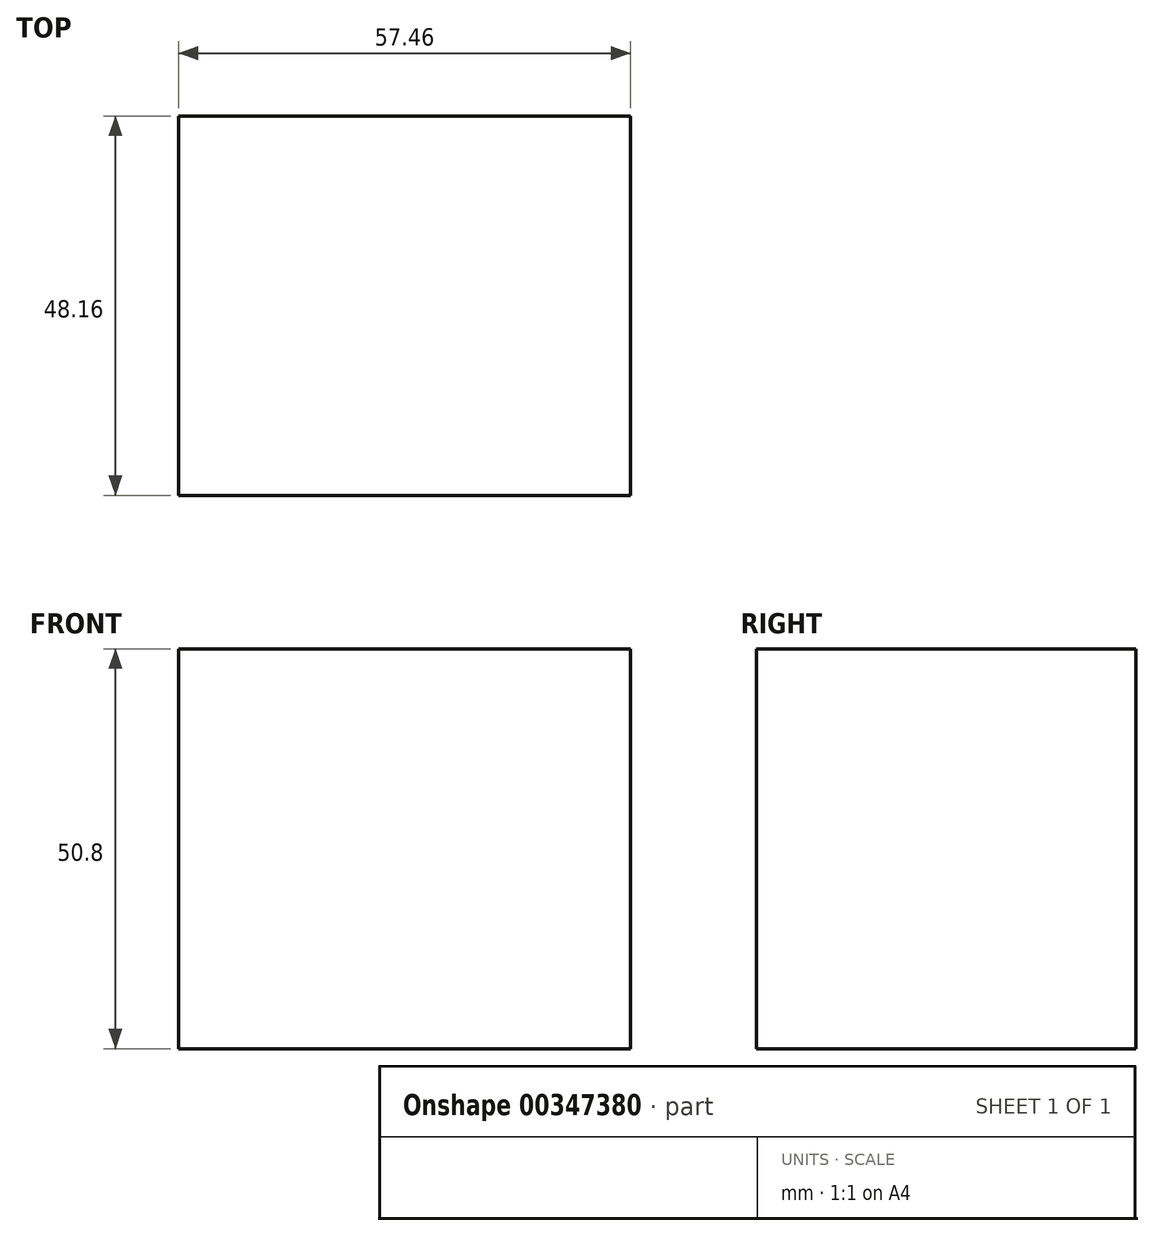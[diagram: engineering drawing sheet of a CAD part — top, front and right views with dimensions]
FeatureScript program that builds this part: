
annotation { "Feature Type Name" : "Feature", "Feature Type Description" : "" }
export const myFeature = defineFeature(function(context is Context, id is Id, definition is map)
    precondition{}
    {
        {
            var Q0;
            Q0=qCreatedBy(makeId("Top.planeOp"),FACE);
            var sketch = newSketch(context, id + "F0", { "sketchPlane" : qUnion([Q0])});
            skLineSegment(sketch, "E0.bottom", {"start": v(0, 0) * mm, "end": v(-57.46, 0) * mm});
            skLineSegment(sketch, "E0.top", {"start": v(0, 48.16) * mm, "end": v(-57.46, 48.16) * mm});
            skLineSegment(sketch, "E0.left", {"start": v(0, 0) * mm, "end": v(0, 48.16) * mm});
            skLineSegment(sketch, "E0.right", {"start": v(-57.46, 0) * mm, "end": v(-57.46, 48.16) * mm});
            skSolve(sketch);
        }
        {
            var Q0;
            Q0 = qSketchRegion(id + "F0", true);
            extrude(context, id + "F1", {"entities" : qUnion([Q0]), "depth" : 50.8 * mm});
        }
    });
